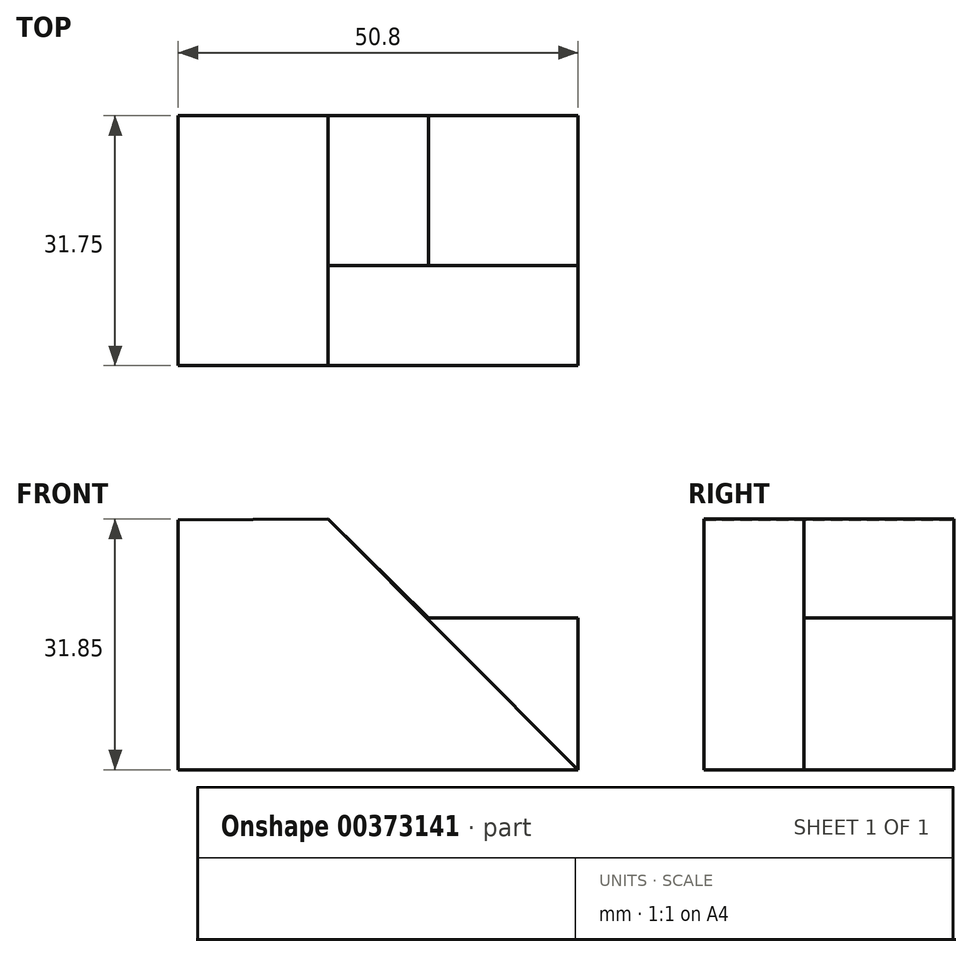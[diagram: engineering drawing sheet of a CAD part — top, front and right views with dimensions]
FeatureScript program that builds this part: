
annotation { "Feature Type Name" : "Feature", "Feature Type Description" : "" }
export const myFeature = defineFeature(function(context is Context, id is Id, definition is map)
    precondition{}
    {
        {
            var Q0;
            Q0=qCreatedBy(makeId("Front.planeOp"),FACE);
            var sketch = newSketch(context, id + "F0", { "sketchPlane" : qUnion([Q0])});
            skLineSegment(sketch, "E0", {"start": v(-29.41, 31.75) * mm, "end": v(-29.41, 0) * mm});
            skLineSegment(sketch, "E1", {"start": v(-29.41, 0) * mm, "end": v(21.39, 0) * mm});
            skLineSegment(sketch, "E2", {"start": v(21.39, 0) * mm, "end": v(21.39, 32.02) * mm});
            skLineSegment(sketch, "E3", {"start": v(21.39, 32.02) * mm, "end": v(-29.41, 31.75) * mm});
            skSolve(sketch);
        }
        {
            var Q0;
            Q0=makeQuery(id+"F0.imprint","IMPRINT",FACE,{"disambiguationData":[TD([[makeQuery(id+"F0.imprint","IMPRINT",EDGE,{"derivedFrom":sQuery(id+"F0.wireOp",EDGE,"E0")}),1.0]])]});
            extrude(context, id + "F1", {"entities" : qUnion([Q0]), "depth" : 31.75 * mm});
        }
        {
            var Q0;
            Q0=makeQuery(id+"F1.opExtrude","CAP_FACE",FACE,{"disambiguationData":[OSD([sQuery(id+"F0.wireOp",EDGE,"E0"),sQuery(id+"F0.wireOp",EDGE,"E1"),sQuery(id+"F0.wireOp",EDGE,"E2"),sQuery(id+"F0.wireOp",EDGE,"E3")])],"isStart":false});
            var sketch = newSketch(context, id + "F2", { "sketchPlane" : qUnion([Q0])});
            skLineSegment(sketch, "E4", {"start": v(-10.36, 31.85) * mm, "end": v(21.39, 0) * mm});
            skSolve(sketch);
        }
        {
            var Q0;
            {var subQ0=sQuery(id+"F2.wireOp",EDGE,"E4");Q0=makeQuery(id+"F2.imprint","IMPRINT",FACE,{"disambiguationData":[TD([[makeQuery(id+"F2.imprint","IMPRINT",EDGE,{"derivedFrom":subQ0}),1.0]])]});}
            var sketch = newSketch(context, id + "F3", { "sketchPlane" : qUnion([Q0])});
            skSolve(sketch);
        }
        {
            var Q0;
            Q0 = qSketchRegion(id + "F3", true);
            var Q1;
            {var subQ0=sQuery(id+"F2.wireOp",EDGE,"E4");Q1=makeQuery(id+"F2.imprint","IMPRINT",FACE,{"disambiguationData":[TD([[makeQuery(id+"F2.imprint","IMPRINT",EDGE,{"derivedFrom":subQ0}),1.0]])]});}
            extrude(context, id + "F4", {"entities" : qUnion([Q0, Q1]), "operationType" : NewBodyOperationType.REMOVE, "oppositeDirection" : true, "depth" : 12.7 * mm});
        }
        {
            var Q0;
            Q0=makeQuery(id+"F1.opExtrude","CAP_FACE",FACE,{"disambiguationData":[OSD([sQuery(id+"F0.wireOp",EDGE,"E0"),sQuery(id+"F0.wireOp",EDGE,"E1"),sQuery(id+"F0.wireOp",EDGE,"E2"),sQuery(id+"F0.wireOp",EDGE,"E3")])],"isStart":true});
            var sketch = newSketch(context, id + "F5", { "sketchPlane" : qUnion([Q0])});
            skLineSegment(sketch, "E5", {"start": v(-21.39, 19.33) * mm, "end": v(-2.4, 19.33) * mm});
            skLineSegment(sketch, "E6", {"start": v(-2.4, 19.33) * mm, "end": v(-2.34, 32.02) * mm});
            skSolve(sketch);
        }
        {
            var Q0;
            {var subQ0=sQuery(id+"F5.wireOp",EDGE,"E5");Q0=makeQuery(id+"F5.imprint","IMPRINT",FACE,{"disambiguationData":[TD([[makeQuery(id+"F5.imprint","IMPRINT",EDGE,{"derivedFrom":subQ0}),1.0]])]});}
            extrude(context, id + "F6", {"entities" : qUnion([Q0]), "operationType" : NewBodyOperationType.REMOVE, "oppositeDirection" : true, "depth" : 31.75 * mm});
        }
        {
            var Q0;
            Q0=makeQuery(id+"F4.boolean.opBoolean","COPY",FACE,{"derivedFrom":makeQuery(id+"F4.opExtrude","CAP_FACE",FACE,{"disambiguationData":[OSD([sQuery(id+"F0.wireOp",EDGE,"E2"),sQuery(id+"F0.wireOp",EDGE,"E3"),sQuery(id+"F2.wireOp",EDGE,"E4")])],"isStart":false})});
            var sketch = newSketch(context, id + "F7", { "sketchPlane" : qUnion([Q0])});
            skLineSegment(sketch, "E7", {"start": v(-10.36, 31.85) * mm, "end": v(2.34, 31.92) * mm});
            skLineSegment(sketch, "E8", {"start": v(2.34, 31.92) * mm, "end": v(2.4, 19.33) * mm});
            skLineSegment(sketch, "E9", {"start": v(2.4, 19.33) * mm, "end": v(-10.36, 31.85) * mm});
            skSolve(sketch);
        }
        {
            var Q0;
            Q0=makeQuery(id+"F7.imprint","IMPRINT",FACE,{"disambiguationData":[TD([[makeQuery(id+"F7.imprint","IMPRINT",EDGE,{"derivedFrom":sQuery(id+"F7.wireOp",EDGE,"E7")}),1.0]])]});
            extrude(context, id + "F8", {"entities" : qUnion([Q0]), "operationType" : NewBodyOperationType.REMOVE, "oppositeDirection" : true, "depth" : 31.75 * mm});
        }
    });
